annotation { "Feature Type Name" : "Feature", "Feature Type Description" : "" }
export const myFeature = defineFeature(function(context is Context, id is Id, definition is map)
    precondition{}
    {
        {
            var Q0;
            Q0=qCreatedBy(makeId("Front.planeOp"),FACE);
            var sketch = newSketch(context, id + "F0", { "sketchPlane" : qUnion([Q0])});
            skCircle(sketch, "E0", {"center": v(0, 0) * mm, "radius": 39.9 * mm});
            skCircle(sketch, "E1", {"center": v(0, 0) * mm, "radius": 47.4 * mm});
            skSolve(sketch);
        }
        {
            var Q0;
            Q0=makeQuery(id+"F0.imprint","IMPRINT",FACE,{"disambiguationData":[TD([[makeQuery(id+"F0.imprint","IMPRINT",EDGE,{"derivedFrom":sQuery(id+"F0.wireOp",EDGE,"E0")}),-1.0]])]});
            extrude(context, id + "F1", {"entities" : qUnion([Q0]), "depth" : 239.9 * mm, "offsetDistance" : 25 * mm});
        }
        {
            var Q0;
            Q0=qCreatedBy(makeId("Front.planeOp"),FACE);
            cPlane(context, id + "F2", {"entities" : qUnion([Q0]), "cplaneType" : CPlaneType.OFFSET, "offset" : 7.5 * mm, "oppositeDirection" : true, "width" : 150 * mm, "height" : 150 * mm});
        }
        {
            var Q0;
            Q0=qCreatedBy(id+"F2.planeOp",FACE);
            var sketch = newSketch(context, id + "F3", { "sketchPlane" : qUnion([Q0])});
            skCircle(sketch, "E2", {"center": v(0, 0) * mm, "radius": 47.4 * mm});
            skCircle(sketch, "E3", {"center": v(154.84, 0) * mm, "radius": 47.4 * mm});
            skSolve(sketch);
        }
        {
            var Q0;
            Q0=makeQuery(id+"F3.imprint","IMPRINT",FACE,{"disambiguationData":[TD([[makeQuery(id+"F3.imprint","IMPRINT",EDGE,{"derivedFrom":sQuery(id+"F3.wireOp",EDGE,"E2")}),1.0]])]});
            var Q1;
            Q1=makeQuery(id+"F3.imprint","IMPRINT",FACE,{"disambiguationData":[TD([[makeQuery(id+"F3.imprint","IMPRINT",EDGE,{"derivedFrom":sQuery(id+"F3.wireOp",EDGE,"E3")}),1.0]])]});
            var Q2;
            Q2=makeQuery(id+"F1.opExtrude","SWEPT_FACE",FACE,{"disambiguationData":[OSD([sQuery(id+"F0.wireOp",EDGE,"E1")])]});
            var Q3;
            Q3=makeQuery(id+"F1.opExtrude","SWEPT_BODY",BODY,{"disambiguationData":[OSD([sQuery(id+"F0.wireOp",EDGE,"E0"),sQuery(id+"F0.wireOp",EDGE,"E1")])]});
            extrude(context, id + "F4", {"entities" : qUnion([Q0, Q1]), "operationType" : NewBodyOperationType.ADD, "depth" : 7.5 * mm, "endBoundEntityFace" : qUnion([Q2]), "endBoundEntityBody" : qUnion([Q3]), "offsetDistance" : 25 * mm});
        }
        {
            var Q0;
            Q0=makeQuery(id+"F4.opExtrude","CAP_FACE",FACE,{"disambiguationData":[OSD([sQuery(id+"F3.wireOp",EDGE,"E3")])],"isStart":false});
            var sketch = newSketch(context, id + "F5", { "sketchPlane" : qUnion([Q0])});
            skCircle(sketch, "E4", {"center": v(154.84, 0) * mm, "radius": 38.75 * mm});
            skCircle(sketch, "E5", {"center": v(154.84, 0) * mm, "radius": 34.75 * mm});
            skSolve(sketch);
        }
        {
            var Q0;
            Q0 = qSketchRegion(id + "F5", true);
            extrude(context, id + "F6", {"entities" : qUnion([Q0]), "operationType" : NewBodyOperationType.ADD, "depth" : 7.5 * mm, "offsetDistance" : 25 * mm});
        }
        {
            var Q0;
            Q0=makeQuery(id+"F1.opExtrude","SWEPT_BODY",BODY,{"disambiguationData":[OSD([sQuery(id+"F0.wireOp",EDGE,"E0"),sQuery(id+"F0.wireOp",EDGE,"E1")])]});
            var Q1;
            Q1=qCreatedBy(makeId("Origin.pointOp"),VERTEX);
            transform(context, id + "F7", {"entities" : qUnion([Q0]), "transformType" : TransformType.SCALE_UNIFORMLY, "scale" : 0.5, "scalePoint" : qUnion([Q1]), "makeCopy" : false});
        }
        {
            var Q0;
            Q0=makeQuery(id+"F4.opExtrude","SWEPT_BODY",BODY,{"disambiguationData":[OSD([sQuery(id+"F3.wireOp",EDGE,"E3")])]});
            var Q1;
            Q1=qCreatedBy(makeId("Origin.pointOp"),VERTEX);
            transform(context, id + "F8", {"entities" : qUnion([Q0]), "transformType" : TransformType.SCALE_UNIFORMLY, "scale" : 0.5, "scalePoint" : qUnion([Q1]), "makeCopy" : false});
        }
        {
            var Q0;
            Q0=makeQuery(id+"F6.boolean.opBoolean","SPLIT",FACE,{"disambiguationData":[TD([makeQuery(id+"F6.opExtrude","SWEPT_FACE",FACE,{"disambiguationData":[OSD([sQuery(id+"F5.wireOp",EDGE,"E5")])]})])],"derivedFrom":makeQuery(id+"F4.opExtrude","CAP_FACE",FACE,{"disambiguationData":[OSD([sQuery(id+"F3.wireOp",EDGE,"E3")])],"isStart":false})});
            var sketch = newSketch(context, id + "F9", { "sketchPlane" : qUnion([Q0])});
            skText(sketch, "E6", { "text": "GB JS", "fontName": "OpenSans-Regular.ttf"});
            const initialGuessF9  = {"E6": [0.0551, -0.007, 1, 0, 0.01302]};
            skSetInitialGuess(sketch, initialGuessF9);
            skSolve(sketch);
        }
        {
            var Q0;
            Q0 = qSketchRegion(id + "F9", true);
            extrude(context, id + "F10", {"entities" : qUnion([Q0]), "depth" : 3 * mm, "offsetDistance" : 25 * mm});
        }
        {
            var Q0;
            Q0=makeQuery(id+"F10.opExtrude","SWEPT_BODY",BODY,{"disambiguationData":[OSD([sQuery(id+"F9.wireOp",EDGE,"E6.sketch_text.stroke-0"),sQuery(id+"F9.wireOp",EDGE,"E6.sketch_text.stroke-1"),sQuery(id+"F9.wireOp",EDGE,"E6.sketch_text.stroke-2"),sQuery(id+"F9.wireOp",EDGE,"E6.sketch_text.stroke-3"),sQuery(id+"F9.wireOp",EDGE,"E6.sketch_text.stroke-4"),sQuery(id+"F9.wireOp",EDGE,"E6.sketch_text.stroke-5"),sQuery(id+"F9.wireOp",EDGE,"E6.sketch_text.stroke-6"),sQuery(id+"F9.wireOp",EDGE,"E6.sketch_text.stroke-7"),sQuery(id+"F9.wireOp",EDGE,"E6.sketch_text.stroke-8"),sQuery(id+"F9.wireOp",EDGE,"E6.sketch_text.stroke-9"),sQuery(id+"F9.wireOp",EDGE,"E6.sketch_text.stroke-10"),sQuery(id+"F9.wireOp",EDGE,"E6.sketch_text.stroke-11"),sQuery(id+"F9.wireOp",EDGE,"E6.sketch_text.stroke-12"),sQuery(id+"F9.wireOp",EDGE,"E6.sketch_text.stroke-13"),sQuery(id+"F9.wireOp",EDGE,"E6.sketch_text.stroke-14"),sQuery(id+"F9.wireOp",EDGE,"E6.sketch_text.stroke-15"),sQuery(id+"F9.wireOp",EDGE,"E6.sketch_text.stroke-16"),sQuery(id+"F9.wireOp",EDGE,"E6.sketch_text.stroke-17"),sQuery(id+"F9.wireOp",EDGE,"E6.sketch_text.stroke-18"),sQuery(id+"F9.wireOp",EDGE,"E6.sketch_text.stroke-19")])]});
            var Q1;
            Q1=makeQuery(id+"F10.opExtrude","SWEPT_BODY",BODY,{"disambiguationData":[OSD([sQuery(id+"F9.wireOp",EDGE,"E6.sketch_text.stroke-20"),sQuery(id+"F9.wireOp",EDGE,"E6.sketch_text.stroke-21"),sQuery(id+"F9.wireOp",EDGE,"E6.sketch_text.stroke-22"),sQuery(id+"F9.wireOp",EDGE,"E6.sketch_text.stroke-23"),sQuery(id+"F9.wireOp",EDGE,"E6.sketch_text.stroke-24"),sQuery(id+"F9.wireOp",EDGE,"E6.sketch_text.stroke-25"),sQuery(id+"F9.wireOp",EDGE,"E6.sketch_text.stroke-26"),sQuery(id+"F9.wireOp",EDGE,"E6.sketch_text.stroke-27"),sQuery(id+"F9.wireOp",EDGE,"E6.sketch_text.stroke-28"),sQuery(id+"F9.wireOp",EDGE,"E6.sketch_text.stroke-29"),sQuery(id+"F9.wireOp",EDGE,"E6.sketch_text.stroke-30"),sQuery(id+"F9.wireOp",EDGE,"E6.sketch_text.stroke-31"),sQuery(id+"F9.wireOp",EDGE,"E6.sketch_text.stroke-32"),sQuery(id+"F9.wireOp",EDGE,"E6.sketch_text.stroke-33"),sQuery(id+"F9.wireOp",EDGE,"E6.sketch_text.stroke-34"),sQuery(id+"F9.wireOp",EDGE,"E6.sketch_text.stroke-35"),sQuery(id+"F9.wireOp",EDGE,"E6.sketch_text.stroke-36"),sQuery(id+"F9.wireOp",EDGE,"E6.sketch_text.stroke-37"),sQuery(id+"F9.wireOp",EDGE,"E6.sketch_text.stroke-38"),sQuery(id+"F9.wireOp",EDGE,"E6.sketch_text.stroke-39"),sQuery(id+"F9.wireOp",EDGE,"E6.sketch_text.stroke-40"),sQuery(id+"F9.wireOp",EDGE,"E6.sketch_text.stroke-41"),sQuery(id+"F9.wireOp",EDGE,"E6.sketch_text.stroke-42"),sQuery(id+"F9.wireOp",EDGE,"E6.sketch_text.stroke-43"),sQuery(id+"F9.wireOp",EDGE,"E6.sketch_text.stroke-44")])]});
            var Q2;
            Q2=makeQuery(id+"F10.opExtrude","SWEPT_BODY",BODY,{"disambiguationData":[OSD([sQuery(id+"F9.wireOp",EDGE,"E6.sketch_text.stroke-45"),sQuery(id+"F9.wireOp",EDGE,"E6.sketch_text.stroke-46"),sQuery(id+"F9.wireOp",EDGE,"E6.sketch_text.stroke-47"),sQuery(id+"F9.wireOp",EDGE,"E6.sketch_text.stroke-48"),sQuery(id+"F9.wireOp",EDGE,"E6.sketch_text.stroke-49"),sQuery(id+"F9.wireOp",EDGE,"E6.sketch_text.stroke-50"),sQuery(id+"F9.wireOp",EDGE,"E6.sketch_text.stroke-51"),sQuery(id+"F9.wireOp",EDGE,"E6.sketch_text.stroke-52"),sQuery(id+"F9.wireOp",EDGE,"E6.sketch_text.stroke-53"),sQuery(id+"F9.wireOp",EDGE,"E6.sketch_text.stroke-54")])]});
            var Q3;
            Q3=makeQuery(id+"F10.opExtrude","SWEPT_BODY",BODY,{"disambiguationData":[OSD([sQuery(id+"F9.wireOp",EDGE,"E6.sketch_text.stroke-55"),sQuery(id+"F9.wireOp",EDGE,"E6.sketch_text.stroke-56"),sQuery(id+"F9.wireOp",EDGE,"E6.sketch_text.stroke-57"),sQuery(id+"F9.wireOp",EDGE,"E6.sketch_text.stroke-58"),sQuery(id+"F9.wireOp",EDGE,"E6.sketch_text.stroke-59"),sQuery(id+"F9.wireOp",EDGE,"E6.sketch_text.stroke-60"),sQuery(id+"F9.wireOp",EDGE,"E6.sketch_text.stroke-61"),sQuery(id+"F9.wireOp",EDGE,"E6.sketch_text.stroke-62"),sQuery(id+"F9.wireOp",EDGE,"E6.sketch_text.stroke-63"),sQuery(id+"F9.wireOp",EDGE,"E6.sketch_text.stroke-64"),sQuery(id+"F9.wireOp",EDGE,"E6.sketch_text.stroke-65"),sQuery(id+"F9.wireOp",EDGE,"E6.sketch_text.stroke-66"),sQuery(id+"F9.wireOp",EDGE,"E6.sketch_text.stroke-67"),sQuery(id+"F9.wireOp",EDGE,"E6.sketch_text.stroke-68"),sQuery(id+"F9.wireOp",EDGE,"E6.sketch_text.stroke-69"),sQuery(id+"F9.wireOp",EDGE,"E6.sketch_text.stroke-70"),sQuery(id+"F9.wireOp",EDGE,"E6.sketch_text.stroke-71"),sQuery(id+"F9.wireOp",EDGE,"E6.sketch_text.stroke-72"),sQuery(id+"F9.wireOp",EDGE,"E6.sketch_text.stroke-73"),sQuery(id+"F9.wireOp",EDGE,"E6.sketch_text.stroke-74"),sQuery(id+"F9.wireOp",EDGE,"E6.sketch_text.stroke-75"),sQuery(id+"F9.wireOp",EDGE,"E6.sketch_text.stroke-76"),sQuery(id+"F9.wireOp",EDGE,"E6.sketch_text.stroke-77"),sQuery(id+"F9.wireOp",EDGE,"E6.sketch_text.stroke-78"),sQuery(id+"F9.wireOp",EDGE,"E6.sketch_text.stroke-79")])]});
            var Q4;
            Q4=qCreatedBy(makeId("Origin.pointOp"),VERTEX);
            transform(context, id + "F11", {"entities" : qUnion([Q0, Q1, Q2, Q3]), "transformType" : TransformType.SCALE_UNIFORMLY, "scale" : 0.5, "scalePoint" : qUnion([Q4]), "makeCopy" : false});
        }
    });